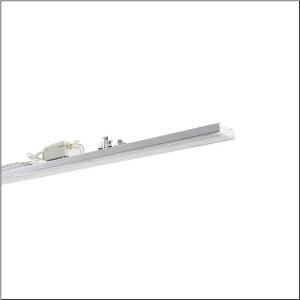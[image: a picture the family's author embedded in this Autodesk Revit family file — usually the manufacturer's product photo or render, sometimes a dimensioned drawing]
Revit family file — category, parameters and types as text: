
# Revit family: licross_21_recessed_ho_52tl12cn495m
name_source: partatom
category: Lighting Fixtures
units: mm (PartAtom-declared; Revit-internal decimal feet)

## family parameters
Cut with Voids When Loaded = No
Host = Face
Light Source = No
Part Type = Normal
Room Calculation Point = No
Round Connector Dimension = Use Diameter
Shared = No

## types (1)
- --- (1 x LED, 10000 lm, 53 W, 4000K)
    Apparent Load = 53 VA
    CIE Flux Codes = 69 91 98 100 100
    Color Rendering = 80
    Color Temperature = 4000K
    Default Elevation = 1800 mm
    Description = Licross 21 Recessed HO, luminaire insert, of sheet steel, galvanised, coil coated, white, length: 1.500mm, width: 66mm, height: 67mm, LED rated luminous flux: 9.990lm, light colour: 840, SDCM (Standard Deviation of Colour Matching)MacAdam ≤ 3 SDCM (initial), control gear: ON/OFF Multilumen, CLOi, with plug, 3-pole, with phase selection, mains connection: 220..240V, AC, 50/60Hz, internal wiring halogen-free, primary optical cover: cover, of PMMA, light emission: direct distribution, primary light characteristic: symmetric, protection rating (complete): IP40, insulation class (complete): insulation class I (protective earthing), certification: CE, ENEC, VDE, UKCA, protection symbol: D if used in an environment without relevant dust loads with corresponding accessories, impact resistance: IK06, permissible ambient temperature for indoor applications: -35..+35°C, corresponds to IFS (International Featured Standards) requirements for safety and quality in the food industry, reducing of maximum allowable ambient temperature of 5°C with ceiling mounting, LABS conformity tested according to VDMA 24364:2018-05, The light source and the operating device comply with the requirements of the Ecodesign Regulation (EU) 2019/2020 and are replaceable in accordance with this regulation, packaging unit: 1 piece
    Height = 58 mm
    Lamp = 1 x LED
    Lamp Light Flux = 10000 lm
    Lamp Power = 53 W
    Lamp count = 1
    Length = 1500 mm
    Luminous efficacy = 189 lm/W
    Manufacturer = Siteco
    ModVariant = No
    Model = 52TL12CN495M
    Mounting Place = Ceiling
    Mounting Type = Pendant
    Number of Poles = 1
    OnlyDefault = Yes
    Power Factor = 1
    Product Name = Licross 21 Recessed HO
    Product group = luminaire insert | ceiling pendant
    ProductGroupID = 901
    Protection Class = Protection class I
    Protection Degree = IP 40
    RLX_Detail_Level = 1
    RLX_Emergency_Light_Flux = 0 lm
    RLX_Emergency_Type = 0
    RLX_Emergency_Type_DB = No
    RlxData = <blob elided: 22589 chars, md5=1bc74fbe>
    Socket = socket
    Standby Power = 0 W
    System Light Flux = 10000 lm
    System Power = 53 W
    Type Comments = factory setting: luminous flux: 100 % | (A | C | E) | 125 mA
    Type Image = l_1296930.jpg
    URL = http://relux.com
    VarID = @adj_111317
    Voltage = 0 V
    Weight = 0.00 kg
    Width = 66 mm

## geometry (parser evidence)
native form markers: Blend x4, Sweep x9
no freeform markers — native parametric forms only
